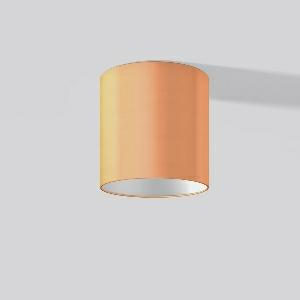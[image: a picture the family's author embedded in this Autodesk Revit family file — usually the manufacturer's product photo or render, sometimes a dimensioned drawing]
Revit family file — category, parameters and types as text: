
# Revit family: toledo_flatliner_901628_002_1_a1e6
name_source: partatom
category: Lighting Fixtures
units: mm (PartAtom-declared; Revit-internal decimal feet)

## family parameters
Cut with Voids When Loaded = No
Host = Face
Light Source = No
Part Type = Normal
Room Calculation Point = No
Round Connector Dimension = Use Diameter
Shared = No

## types (1)
- 982299.002 (1 x LED Modul 840, 360 lm, 4000)
    Apparent Load = 5 VA
    CIE Flux Codes = 56 78 92 81 100
    Color Rendering = 80
    Color Temperature = 4000
    Default Elevation = 1800 mm
    Description = Series: TOLEDO FLATLINER
Decorative ceiling luminaire for interior decoration. Base luminaire prepared for the installation of fabric lampshade. Cylinder housing sheet steel, powder-coated. Housing: die cast aluminium and sheet steel, powder-coated. Bezel ring: die-cast aluminium, powder-coated. Lightguide and diffuser made of non-yellowing plastic (PMMA) opal matt. Modular design: With the basic luminaire, a square or cylindrical fabric lampshade must always be ordered separately. Fabric lampshades can be fitted to the basic luminaire without tools. Order satin finish diffuser as separate accessory. 
Colour: white
Diameter: 160 mm
Height: 65 mm
Lamp: LED
Socket: without socket
Colour temperature: 4000K
Colour rendering index (CRI): 80
System power: 5 W
Rated luminous flux: 360 lm
Luminous efficiency: 72 lm/W
Control gear: Regulated power supply
Protection class: II
Type of protection: IP 40
    Height = 65 mm
    Lamp = 1 x LED Modul 840
    Lamp Light Flux = 360 lm
    Lamp count = 1
    Length = 160 mm
    Lifetime = 50000 h
    Luminous efficacy = 72 lm/W
    Manufacturer = RZB
    ModVariant = No
    Model = 901628.002.1
    Mounting Place = Ceiling
    Mounting Type = Surface mounted
    Number of Poles = 1
    OnlyDefault = Yes
    Power Factor = 1
    Product Name = TOLEDO FLATLINER
    Product group = Surface mounted ceiling Fabric lampshade luminaires
    ProductGroupID = 313
    Protection Class = Protection class II
    Protection Degree = IP 40
    RLX_Detail_Level = 1
    RLX_Emergency_Light_Flux = 0 lm
    RLX_Emergency_Type = 0
    RLX_Emergency_Type_DB = No
    RlxData = <blob elided: 62257 chars, md5=01216cb5>
    Socket = socket
    Standby Power = 0 W
    System Light Flux = 360 lm
    System Power = 5 W
    Type Image = toledo_flatliner_anbau_rund_orange_odeckel.jpg
    URL = http://relux.com
    VarID = 982299_002_f7b2
    Voltage = 230 V
    Voltage Range = 220-240 V
    Weight = 0.00 kg
    Width = 0 mm  [stored 0 ft]

note: [stored X ft] marks values corroborated as IEEE doubles in the binary element streams (Revit-internal decimal feet)

## geometry (parser evidence)
native form markers: Blend x4, Sweep x13
no freeform markers — native parametric forms only
